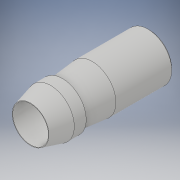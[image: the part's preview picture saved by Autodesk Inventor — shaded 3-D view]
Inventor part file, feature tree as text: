
AUTODESK INVENTOR PART (.ipt)
format: ipt  version: 2019 (Build 230136000, 136)  size: 135,168 bytes
history: native  units: mm
features: other x1, chamfer x1, sketch x1
ambient origin geometry x8: Origin, YZ Plane, XZ Plane, XY Plane, X Axis, Y Axis, Z Axis, Center Point
bodies: Solide1 (feature_tree)
feature tree (3):
  other  "Révolution1"
  chamfer  "Chanfrein1"  Distance=12.0mm
  sketch  "Esquisse1"
